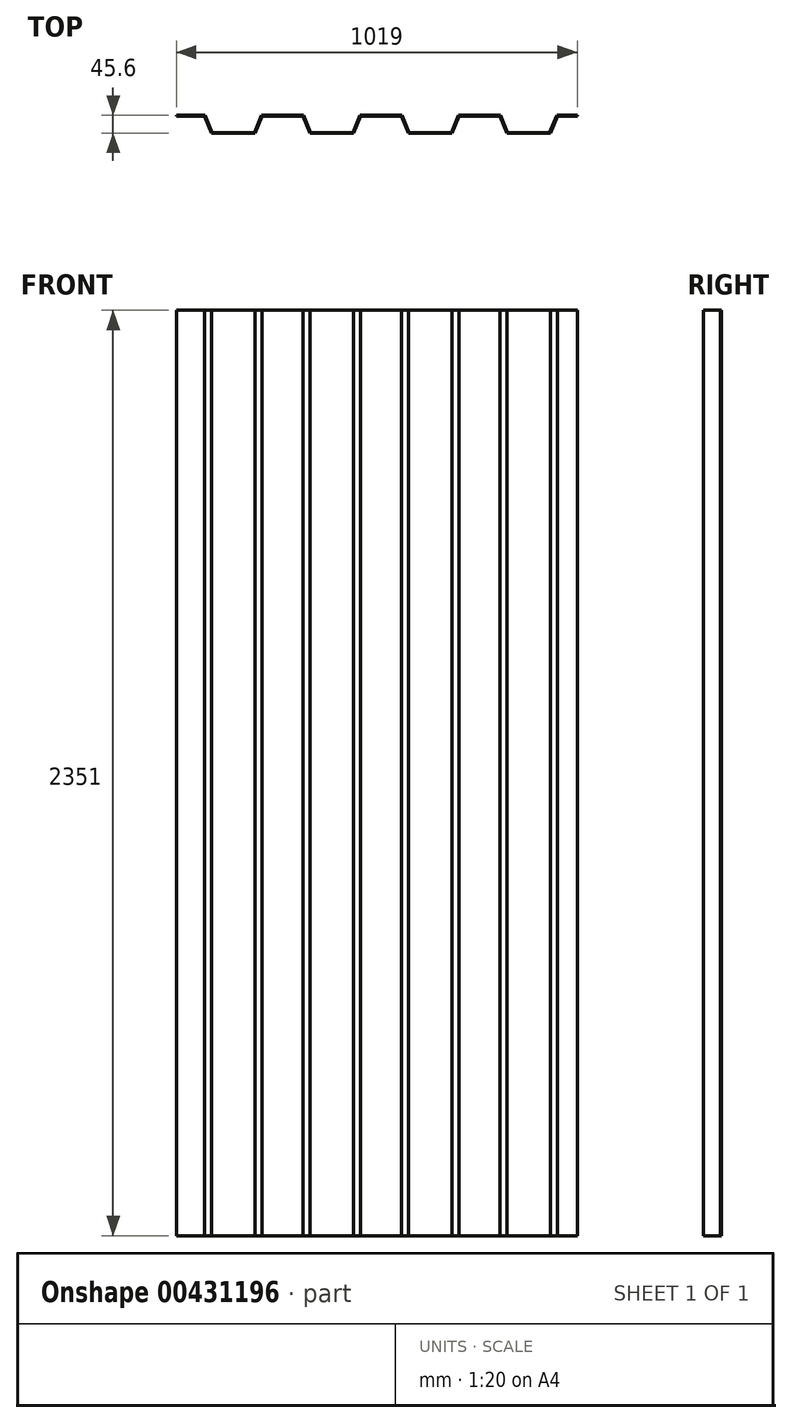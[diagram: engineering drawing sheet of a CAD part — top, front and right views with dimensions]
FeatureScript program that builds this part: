
annotation { "Feature Type Name" : "Feature", "Feature Type Description" : "" }
export const myFeature = defineFeature(function(context is Context, id is Id, definition is map)
    precondition{}
    {
        {
            var Q0;
            Q0=qCreatedBy(makeId("Top.planeOp"),FACE);
            var sketch = newSketch(context, id + "F0", { "sketchPlane" : qUnion([Q0])});
            skLineSegment(sketch, "E0", {"start": v(0, 0) * mm, "end": v(72, 0) * mm});
            skLineSegment(sketch, "E1", {"start": v(90, -43.6) * mm, "end": v(200, -43.6) * mm});
            skLineSegment(sketch, "E2", {"start": v(218, 0) * mm, "end": v(322, 0) * mm});
            skLineSegment(sketch, "E3", {"start": v(72, 0) * mm, "end": v(90, -43.6) * mm});
            skLineSegment(sketch, "E4", {"start": v(200, -43.6) * mm, "end": v(218, 0) * mm});
            skLineSegment(sketch, "E5", {"start": v(322, 0) * mm, "end": v(340, -43.6) * mm});
            skLineSegment(sketch, "E6.0", {"start": v(0, 2) * mm, "end": v(73.34, 2) * mm});
            skLineSegment(sketch, "E7.0", {"start": v(198.66, -41.6) * mm, "end": v(216.66, 2) * mm});
            skLineSegment(sketch, "E8.0", {"start": v(216.66, 2) * mm, "end": v(323.34, 2) * mm});
            skLineSegment(sketch, "E9.0", {"start": v(323.34, 2) * mm, "end": v(341.34, -41.6) * mm});
            skLineSegment(sketch, "E10", {"start": v(0, 0) * mm, "end": v(0, 2) * mm});
            skLineSegment(sketch, "E11", {"start": v(340, -43.6) * mm, "end": v(450, -43.6) * mm});
            skLineSegment(sketch, "E12", {"start": v(468, 0) * mm, "end": v(572, 0) * mm});
            skLineSegment(sketch, "E13", {"start": v(450, -43.6) * mm, "end": v(468, 0) * mm});
            skLineSegment(sketch, "E14", {"start": v(572, 0) * mm, "end": v(590, -43.6) * mm});
            skLineSegment(sketch, "E15.0", {"start": v(341.34, -41.6) * mm, "end": v(448.66, -41.6) * mm});
            skLineSegment(sketch, "E16.0", {"start": v(448.66, -41.6) * mm, "end": v(466.66, 2) * mm});
            skLineSegment(sketch, "E17.0", {"start": v(466.66, 2) * mm, "end": v(573.34, 2) * mm});
            skLineSegment(sketch, "E18.0", {"start": v(573.34, 2) * mm, "end": v(591.34, -41.6) * mm});
            skLineSegment(sketch, "E19", {"start": v(590, -43.6) * mm, "end": v(700, -43.6) * mm});
            skLineSegment(sketch, "E20", {"start": v(700, -43.6) * mm, "end": v(718, 0) * mm});
            skLineSegment(sketch, "E21.0", {"start": v(591.34, -41.6) * mm, "end": v(698.66, -41.6) * mm});
            skLineSegment(sketch, "E22.0", {"start": v(698.66, -41.6) * mm, "end": v(716.66, 2) * mm});
            skLineSegment(sketch, "E23.0", {"start": v(91.34, -41.6) * mm, "end": v(198.66, -41.6) * mm});
            skLineSegment(sketch, "E24.0", {"start": v(73.34, 2) * mm, "end": v(91.34, -41.6) * mm});
            skLineSegment(sketch, "E25", {"start": v(718, 0) * mm, "end": v(822, 0) * mm});
            skLineSegment(sketch, "E26", {"start": v(822, 0) * mm, "end": v(840, -43.6) * mm});
            skLineSegment(sketch, "E27.0", {"start": v(716.66, 2) * mm, "end": v(823.34, 2) * mm});
            skLineSegment(sketch, "E28.0", {"start": v(823.34, 2) * mm, "end": v(841.34, -41.6) * mm});
            skLineSegment(sketch, "E29", {"start": v(840, -43.6) * mm, "end": v(950, -43.6) * mm});
            skLineSegment(sketch, "E30", {"start": v(950, -43.6) * mm, "end": v(968, 0) * mm});
            skLineSegment(sketch, "E31.0", {"start": v(841.34, -41.6) * mm, "end": v(948.66, -41.6) * mm});
            skLineSegment(sketch, "E32.0", {"start": v(948.66, -41.6) * mm, "end": v(966.66, 2) * mm});
            skLineSegment(sketch, "E33", {"start": v(968, 0) * mm, "end": v(1019, 0) * mm});
            skLineSegment(sketch, "E34", {"start": v(1019, 0) * mm, "end": v(1019, 2) * mm});
            skLineSegment(sketch, "E35", {"start": v(1019, 2) * mm, "end": v(966.66, 2) * mm});
            skSolve(sketch);
        }
        {
            var Q0;
            Q0=makeQuery(id+"F0.imprint","IMPRINT",FACE,{"disambiguationData":[TD([[makeQuery(id+"F0.imprint","IMPRINT",EDGE,{"derivedFrom":sQuery(id+"F0.wireOp",EDGE,"E0")}),1.0]])]});
            extrude(context, id + "F1", {"entities" : qUnion([Q0]), "depth" : 2351 * mm});
        }
    });
